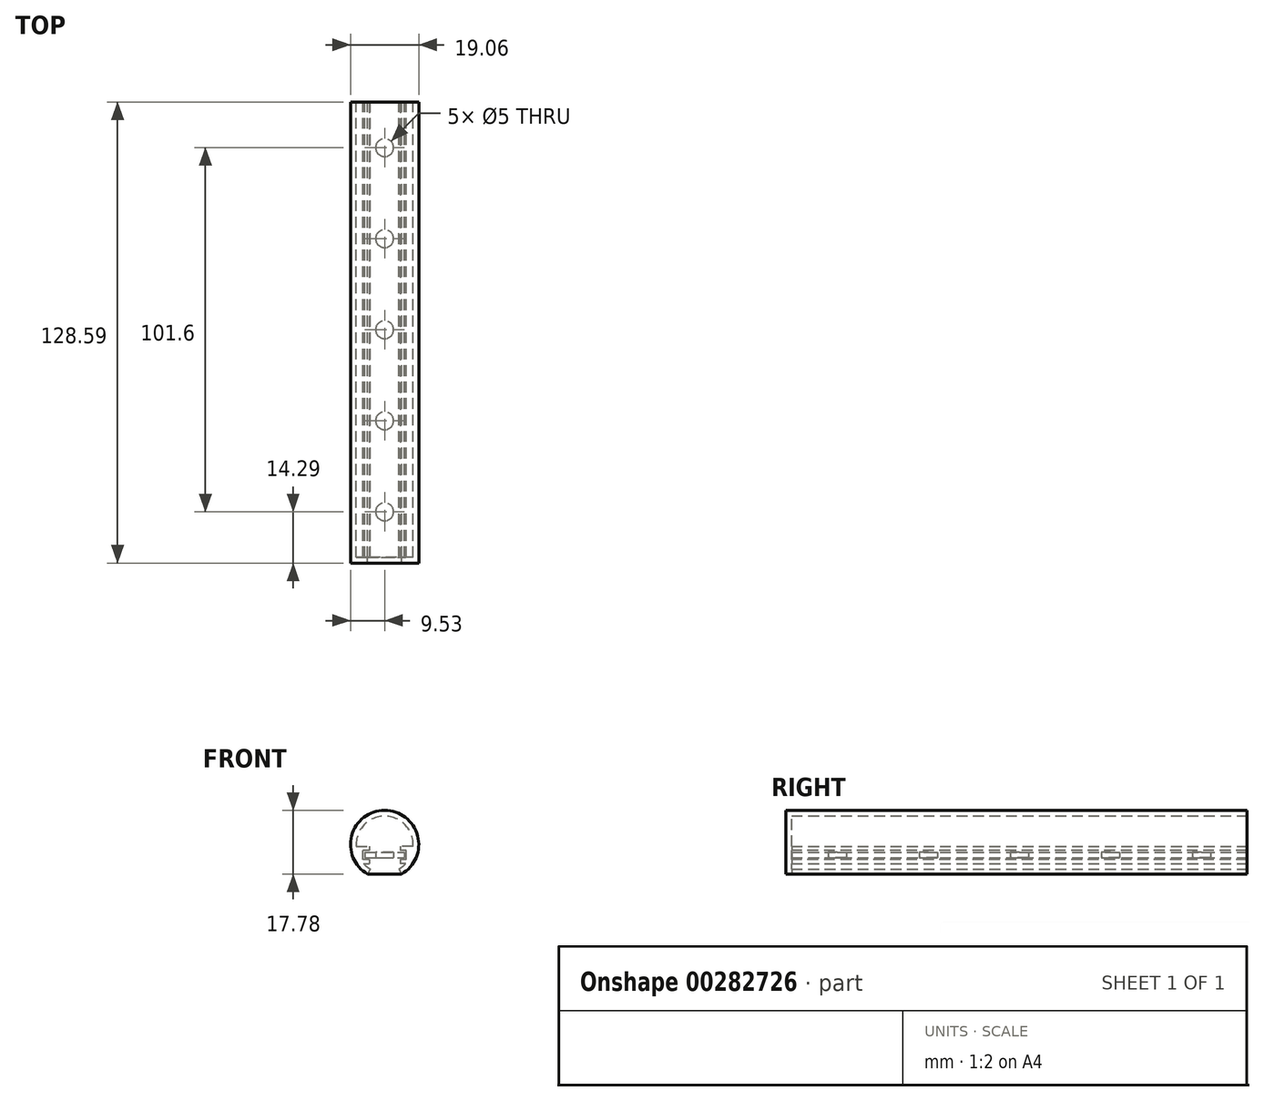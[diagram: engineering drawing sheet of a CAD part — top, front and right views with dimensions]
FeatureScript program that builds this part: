
annotation { "Feature Type Name" : "Feature", "Feature Type Description" : "" }
export const myFeature = defineFeature(function(context is Context, id is Id, definition is map)
    precondition{}
    {
        {
            var Q0;
            Q0=qCreatedBy(makeId("Front.planeOp"),FACE);
            var sketch = newSketch(context, id + "F0", { "sketchPlane" : qUnion([Q0])});
            skCircle(sketch, "E0", {"center": v(0, 0) * mm, "radius": 7.94 * mm});
            skCircle(sketch, "E1", {"center": v(0, 0) * mm, "radius": 9.53 * mm});
            skLineSegment(sketch, "E2", {"start": v(0, 0) * mm, "end": v(0, -14.35) * mm, "construction": true});
            skLineSegment(sketch, "E3", {"start": v(0, 0) * mm, "end": v(3.97, -6.87) * mm, "construction": true});
            skLineSegment(sketch, "E4", {"start": v(3.97, -6.87) * mm, "end": v(4.76, -8.25) * mm});
            skLineSegment(sketch, "E5.MirrorCS", {"start": v(-3.97, -6.87) * mm, "end": v(-4.76, -8.25) * mm});
            skLineSegment(sketch, "E6.MirrorCS", {"start": v(0, 0) * mm, "end": v(-3.97, -6.87) * mm, "construction": true});
            skLineSegment(sketch, "E7.bottom", {"start": v(7.92, -0.52) * mm, "end": v(4.33, -0.52) * mm});
            skLineSegment(sketch, "E7.top", {"start": v(5.92, -5.29) * mm, "end": v(4.33, -5.29) * mm});
            skLineSegment(sketch, "E7.right", {"start": v(4.33, -0.52) * mm, "end": v(4.33, -5.29) * mm});
            skLineSegment(sketch, "E8.MirrorCS", {"start": v(-7.92, -0.52) * mm, "end": v(-4.33, -0.52) * mm});
            skLineSegment(sketch, "E9.MirrorCS", {"start": v(-4.33, -0.52) * mm, "end": v(-4.33, -5.29) * mm});
            skLineSegment(sketch, "E10.MirrorCS", {"start": v(-5.92, -5.29) * mm, "end": v(-4.33, -5.29) * mm});
            skSolve(sketch);
        }
        {
            var Q0;
            {var subQ3=sQuery(id+"F0.wireOp",EDGE,"E4");Q0=makeQuery(id+"F0.imprint","IMPRINT",FACE,{"disambiguationData":[TD([[makeQuery(id+"F0.imprint","IMPRINT",EDGE,{"derivedFrom":subQ3}),1.0]])]});}
            var Q1;
            {var subQ0=sQuery(id+"F0.wireOp",EDGE,"E8.MirrorCS");Q1=makeQuery(id+"F0.imprint","IMPRINT",FACE,{"disambiguationData":[TD([[makeQuery(id+"F0.imprint","IMPRINT",EDGE,{"derivedFrom":subQ0}),-1.0]])]});}
            var Q2;
            {var subQ0=sQuery(id+"F0.wireOp",EDGE,"E7.bottom");Q2=makeQuery(id+"F0.imprint","IMPRINT",FACE,{"disambiguationData":[TD([[makeQuery(id+"F0.imprint","IMPRINT",EDGE,{"derivedFrom":subQ0}),1.0]])]});}
            extrude(context, id + "F1", {"entities" : qUnion([Q0, Q1, Q2]), "depth" : 127 * mm});
        }
        {
            var Q0;
            Q0=makeQuery(id+"F1.opExtrude","CAP_FACE",FACE,{"disambiguationData":[OSD([sQuery(id+"F0.wireOp",EDGE,"E0"),sQuery(id+"F0.wireOp",EDGE,"E1"),sQuery(id+"F0.wireOp",EDGE,"E4"),sQuery(id+"F0.wireOp",EDGE,"E5.MirrorCS"),sQuery(id+"F0.wireOp",EDGE,"E7.bottom"),sQuery(id+"F0.wireOp",EDGE,"E7.top"),sQuery(id+"F0.wireOp",EDGE,"E7.right"),sQuery(id+"F0.wireOp",EDGE,"E8.MirrorCS"),sQuery(id+"F0.wireOp",EDGE,"E9.MirrorCS"),sQuery(id+"F0.wireOp",EDGE,"E10.MirrorCS")])],"isStart":true});
            var sketch = newSketch(context, id + "F2", { "sketchPlane" : qUnion([Q0])});
            skLineSegment(sketch, "E11.bottom", {"start": v(5.53, -2.11) * mm, "end": v(-5.53, -2.11) * mm});
            skLineSegment(sketch, "E11.top", {"start": v(5.53, -3.7) * mm, "end": v(-5.53, -3.7) * mm});
            skLineSegment(sketch, "E11.left", {"start": v(5.53, -2.11) * mm, "end": v(5.53, -3.7) * mm});
            skLineSegment(sketch, "E11.right", {"start": v(-5.53, -2.11) * mm, "end": v(-5.53, -3.7) * mm});
            skPoint(sketch, "E11.middle", {"position": v(0, -2.9) * mm});
            skPoint(sketch, "E11.middle.positionSnap0", {"position": v(-4.33, -2.9) * mm});
            skPoint(sketch, "E11.centerSnap0", {"position": v(-4.33, -2.9) * mm});
            skSolve(sketch);
        }
        {
            var Q0;
            {var subQ0=sQuery(id+"F2.wireOp",EDGE,"E11.bottom");var subQ1=makeQuery(id+"F1.opExtrude","CAP_EDGE",EDGE,{"disambiguationData":[OSD([sQuery(id+"F0.wireOp",EDGE,"E9.MirrorCS")])],"isStart":true});var subQ2=makeQuery(id+"F2.imprint","INTERSECT",VERTEX,{"derivedFrom":[subQ1,subQ0]});Q0=makeQuery(id+"F2.imprint","IMPRINT",FACE,{"disambiguationData":[TD([[makeQuery(id+"F2.imprint","IMPRINT",EDGE,{"disambiguationData":[TD([[subQ2,-1.0]])],"derivedFrom":subQ0}),1.0]])]});}
            var Q1;
            {var subQ0=sQuery(id+"F2.wireOp",EDGE,"E11.right");Q1=makeQuery(id+"F2.imprint","IMPRINT",FACE,{"disambiguationData":[TD([[makeQuery(id+"F2.imprint","IMPRINT",EDGE,{"derivedFrom":subQ0}),1.0]])]});}
            var Q2;
            {var subQ0=sQuery(id+"F2.wireOp",EDGE,"E11.left");Q2=makeQuery(id+"F2.imprint","IMPRINT",FACE,{"disambiguationData":[TD([[makeQuery(id+"F2.imprint","IMPRINT",EDGE,{"derivedFrom":subQ0}),-1.0]])]});}
            var Q3;
            Q3=makeQuery(id+"F1.opExtrude","CAP_FACE",FACE,{"disambiguationData":[OSD([sQuery(id+"F0.wireOp",EDGE,"E0"),sQuery(id+"F0.wireOp",EDGE,"E1"),sQuery(id+"F0.wireOp",EDGE,"E4"),sQuery(id+"F0.wireOp",EDGE,"E5.MirrorCS"),sQuery(id+"F0.wireOp",EDGE,"E7.bottom"),sQuery(id+"F0.wireOp",EDGE,"E7.top"),sQuery(id+"F0.wireOp",EDGE,"E7.right"),sQuery(id+"F0.wireOp",EDGE,"E8.MirrorCS"),sQuery(id+"F0.wireOp",EDGE,"E9.MirrorCS"),sQuery(id+"F0.wireOp",EDGE,"E10.MirrorCS")])],"isStart":false});
            extrude(context, id + "F3", {"entities" : qUnion([Q0, Q1, Q2]), "endBound" : BoundingType.UP_TO_SURFACE, "oppositeDirection" : true, "endBoundEntityFace" : qUnion([Q3]), "depth" : 25.4 * mm});
        }
        {
            var Q0;
            Q0=makeQuery(id+"F3.opExtrude","SWEPT_BODY",BODY,{"disambiguationData":[OSD([sQuery(id+"F2.wireOp",EDGE,"E11.bottom"),sQuery(id+"F2.wireOp",EDGE,"E11.top"),sQuery(id+"F2.wireOp",EDGE,"E11.left"),sQuery(id+"F2.wireOp",EDGE,"E11.right")])]});
            var Q1;
            Q1=makeQuery(id+"F1.opExtrude","SWEPT_BODY",BODY,{"disambiguationData":[OSD([sQuery(id+"F0.wireOp",EDGE,"E0"),sQuery(id+"F0.wireOp",EDGE,"E1"),sQuery(id+"F0.wireOp",EDGE,"E4"),sQuery(id+"F0.wireOp",EDGE,"E5.MirrorCS"),sQuery(id+"F0.wireOp",EDGE,"E7.bottom"),sQuery(id+"F0.wireOp",EDGE,"E7.top"),sQuery(id+"F0.wireOp",EDGE,"E7.right"),sQuery(id+"F0.wireOp",EDGE,"E8.MirrorCS"),sQuery(id+"F0.wireOp",EDGE,"E9.MirrorCS"),sQuery(id+"F0.wireOp",EDGE,"E10.MirrorCS")])]});
            booleanBodies(context, id + "F4", {"operationType" : BooleanOperationType.SUBTRACTION, "tools" : qUnion([Q0]), "targets" : qUnion([Q1]), "offset" : true, "offsetAll" : true, "offsetDistance" : 0.5 * mm, "keepTools" : true});
        }
        {
            var Q0;
            Q0=makeQuery(id+"F1.opExtrude","CAP_FACE",FACE,{"disambiguationData":[OSD([sQuery(id+"F0.wireOp",EDGE,"E0"),sQuery(id+"F0.wireOp",EDGE,"E1"),sQuery(id+"F0.wireOp",EDGE,"E4"),sQuery(id+"F0.wireOp",EDGE,"E5.MirrorCS"),sQuery(id+"F0.wireOp",EDGE,"E7.bottom"),sQuery(id+"F0.wireOp",EDGE,"E7.top"),sQuery(id+"F0.wireOp",EDGE,"E7.right"),sQuery(id+"F0.wireOp",EDGE,"E8.MirrorCS"),sQuery(id+"F0.wireOp",EDGE,"E9.MirrorCS"),sQuery(id+"F0.wireOp",EDGE,"E10.MirrorCS")])],"isStart":false});
            var sketch = newSketch(context, id + "F5", { "sketchPlane" : qUnion([Q0])});
            skArc(sketch, "E12.0", {"start": v(4.76, -8.25) * mm, "mid": v(0, 9.52) * mm, "end": v(-4.76, -8.25) * mm});
            skLineSegment(sketch, "E13", {"start": v(-4.76, -8.25) * mm, "end": v(4.76, -8.25) * mm});
            skSolve(sketch);
        }
        {
            var Q0;
            Q0 = qSketchRegion(id + "F5", true);
            extrude(context, id + "F6", {"entities" : qUnion([Q0]), "operationType" : NewBodyOperationType.ADD, "depth" : 1.59 * mm});
        }
        {
            var Q0;
            Q0=makeQuery(id+"F3.opExtrude","SWEPT_FACE",FACE,{"disambiguationData":[OSD([sQuery(id+"F2.wireOp",EDGE,"E11.top")])]});
            var sketch = newSketch(context, id + "F7", { "sketchPlane" : qUnion([Q0])});
            skCircle(sketch, "E14", {"center": v(0, 12.7) * mm, "radius": 2.5 * mm});
            skCircle(sketch, "E15.0.1.0", {"center": v(0, 38.1) * mm, "radius": 2.5 * mm});
            skCircle(sketch, "E15.0.2.0", {"center": v(0, 63.5) * mm, "radius": 2.5 * mm});
            skCircle(sketch, "E15.0.3.0", {"center": v(0, 88.9) * mm, "radius": 2.5 * mm});
            skCircle(sketch, "E15.0.4.0", {"center": v(0, 114.3) * mm, "radius": 2.5 * mm});
            skLineSegment(sketch, "E15.direction1", {"start": v(0, 12.7) * mm, "end": v(25.4, 12.7) * mm, "construction": true});
            skLineSegment(sketch, "E15.direction2", {"start": v(0, 12.7) * mm, "end": v(0, 38.1) * mm, "construction": true});
            skSolve(sketch);
        }
        {
            var Q0;
            Q0 = qSketchRegion(id + "F7", true);
            extrude(context, id + "F8", {"entities" : qUnion([Q0]), "operationType" : NewBodyOperationType.REMOVE, "endBound" : BoundingType.UP_TO_NEXT, "oppositeDirection" : true, "depth" : 25.4 * mm});
        }
    });
